# Revit family: Pendant Light - Disk
name_source: partatom
category: Lighting Fixtures
revit_build: Autodesk Revit Architecture 2012 (Build: 20110210_1515)
units: mm (PartAtom-declared; Revit-internal decimal feet)

## types (4) — shared parameters
Assembly Code = D5020220
Ballast Number of Poles = 1
Ceiling Mount Material = Metal - Chrome
Color Filter = 16777215
Dimming Lamp Color Temperature Shift = <None>
Drop From Ceiling = 2' - 0"
Emit Shape Visible in Rendering = No
Emit from Circle Diameter = 0' - 9"
Fixture Material = Plastic - Blue
Fixture Radius = 0' - 4 1/2"
Glass Material = Glass - Clear, Grey
Glass Radius = 0' - 9"
Light Source Symbol Size = 2' - 0"
Load Classification = Lighting - Dwelling Unit

## per-type parameters (varying)
| type | Apparent Load | Ballast Voltage | Lamp | Type Comments |
| 100W - 277V | 100 VA | 277 V | A-19 | 3.5" Min.Radius |
| 150W - 120V | 150 VA | 120 V | A-21 |  |
| 150W - 277V | 150 VA | 277 V | A-21 |  |
| 100W - 120V | 100 VA | 120 V | A-19 | 3.5" Min.Radius |

## geometry (parser evidence)
native form markers: Sweep x1
no freeform markers — native parametric forms only
